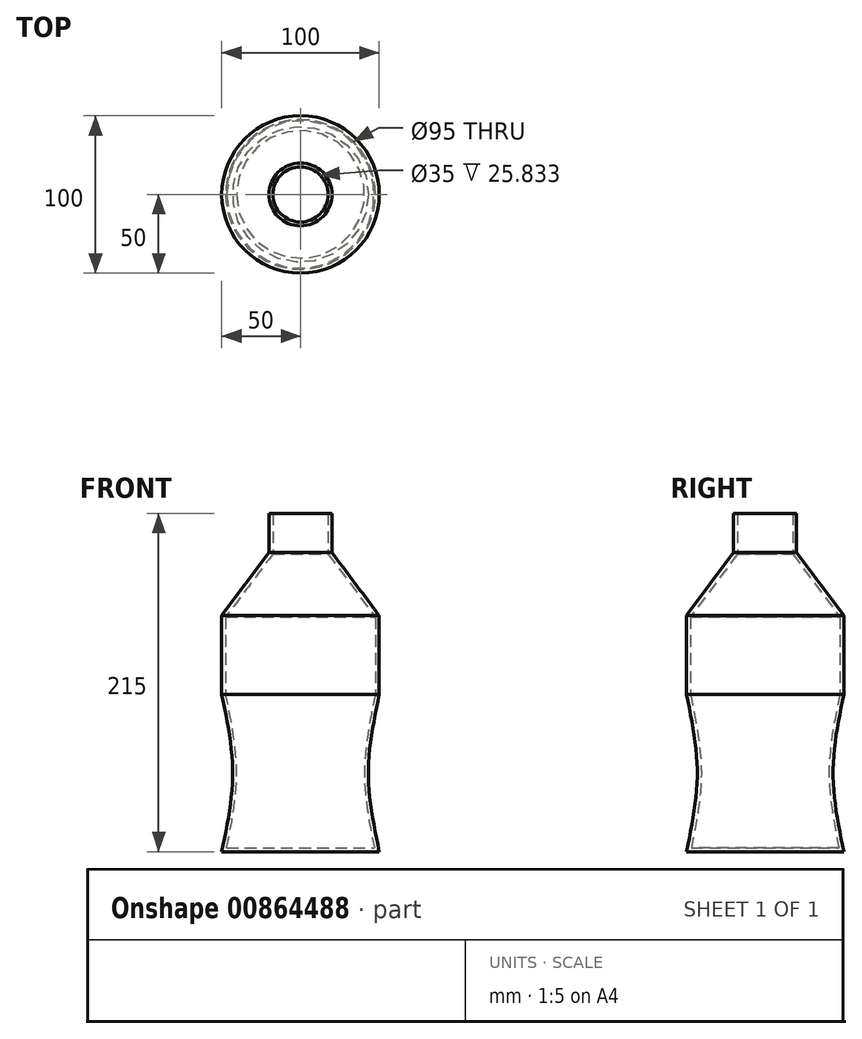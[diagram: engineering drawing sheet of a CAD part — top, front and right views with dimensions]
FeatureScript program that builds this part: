
annotation { "Feature Type Name" : "Feature", "Feature Type Description" : "" }
export const myFeature = defineFeature(function(context is Context, id is Id, definition is map)
    precondition{}
    {
        {
            var Q0;
            Q0=qCreatedBy(makeId("Top.planeOp"),FACE);
            var sketch = newSketch(context, id + "F0", { "sketchPlane" : qUnion([Q0])});
            skCircle(sketch, "E0", {"center": v(0, 0) * mm, "radius": 50 * mm});
            skSolve(sketch);
        }
        {
            var Q0;
            Q0=qCreatedBy(makeId("Top.planeOp"),FACE);
            cPlane(context, id + "F1", {"entities" : qUnion([Q0]), "cplaneType" : CPlaneType.OFFSET, "offset" : 50 * mm, "width" : 150 * mm, "height" : 150 * mm});
        }
        {
            var Q0;
            Q0=qCreatedBy(id+"F1.planeOp",FACE);
            var sketch = newSketch(context, id + "F2", { "sketchPlane" : qUnion([Q0])});
            skCircle(sketch, "E1", {"center": v(0, 0) * mm, "radius": 43.1 * mm});
            skSolve(sketch);
        }
        {
            var Q0;
            Q0=qCreatedBy(id+"F1.planeOp",FACE);
            cPlane(context, id + "F3", {"entities" : qUnion([Q0]), "cplaneType" : CPlaneType.OFFSET, "offset" : 50 * mm, "width" : 150 * mm, "height" : 150 * mm});
        }
        {
            var Q0;
            Q0=qCreatedBy(id+"F3.planeOp",FACE);
            cPlane(context, id + "F4", {"entities" : qUnion([Q0]), "cplaneType" : CPlaneType.OFFSET, "offset" : 50 * mm, "width" : 150 * mm, "height" : 150 * mm});
        }
        {
            var Q0;
            Q0=qCreatedBy(id+"F3.planeOp",FACE);
            var sketch = newSketch(context, id + "F5", { "sketchPlane" : qUnion([Q0])});
            skCircle(sketch, "E2", {"center": v(0, 0) * mm, "radius": 50 * mm});
            skSolve(sketch);
        }
        {
            var Q0;
            Q0=qCreatedBy(id+"F4.planeOp",FACE);
            var sketch = newSketch(context, id + "F6", { "sketchPlane" : qUnion([Q0])});
            skCircle(sketch, "E3", {"center": v(0, 0) * mm, "radius": 50 * mm});
            skSolve(sketch);
        }
        {
            var Q0;
            Q0=qCreatedBy(id+"F4.planeOp",FACE);
            cPlane(context, id + "F7", {"entities" : qUnion([Q0]), "cplaneType" : CPlaneType.OFFSET, "offset" : 40 * mm, "width" : 150 * mm, "height" : 150 * mm});
        }
        {
            var Q0;
            Q0=qCreatedBy(id+"F7.planeOp",FACE);
            var sketch = newSketch(context, id + "F8", { "sketchPlane" : qUnion([Q0])});
            skCircle(sketch, "E4", {"center": v(0, 0) * mm, "radius": 20 * mm});
            skSolve(sketch);
        }
        {
            var Q0;
            Q0=makeQuery(id+"F0.imprint","IMPRINT",FACE,{"disambiguationData":[TD([[makeQuery(id+"F0.imprint","IMPRINT",EDGE,{"derivedFrom":sQuery(id+"F0.wireOp",EDGE,"E0")}),1.0]])]});
            var Q1;
            Q1=makeQuery(id+"F2.imprint","IMPRINT",FACE,{"disambiguationData":[TD([[makeQuery(id+"F2.imprint","IMPRINT",EDGE,{"derivedFrom":sQuery(id+"F2.wireOp",EDGE,"E1")}),1.0]])]});
            var Q2;
            Q2=makeQuery(id+"F5.imprint","IMPRINT",FACE,{"disambiguationData":[TD([[makeQuery(id+"F5.imprint","IMPRINT",EDGE,{"derivedFrom":sQuery(id+"F5.wireOp",EDGE,"E2")}),1.0]])]});
            loft(context, id + "F9", {"sheetProfilesArray" : [{ "sheetProfileEntities" : qUnion([Q0]) }, { "sheetProfileEntities" : qUnion([Q1]) }, { "sheetProfileEntities" : qUnion([Q2]) }]});
        }
        {
            var Q0;
            Q0=makeQuery(id+"F5.imprint","IMPRINT",FACE,{"disambiguationData":[TD([[makeQuery(id+"F5.imprint","IMPRINT",EDGE,{"derivedFrom":sQuery(id+"F5.wireOp",EDGE,"E2")}),1.0]])]});
            extrude(context, id + "F10", {"entities" : qUnion([Q0]), "operationType" : NewBodyOperationType.ADD, "depth" : 50 * mm, "offsetDistance" : 25 * mm});
        }
        {
            var Q1;
            Q1=makeQuery(id+"F6.imprint","IMPRINT",FACE,{"disambiguationData":[TD([[makeQuery(id+"F6.imprint","IMPRINT",EDGE,{"derivedFrom":sQuery(id+"F6.wireOp",EDGE,"E3")}),1.0]])]});
            var Q2;
            Q2=makeQuery(id+"F8.imprint","IMPRINT",FACE,{"disambiguationData":[TD([[makeQuery(id+"F8.imprint","IMPRINT",EDGE,{"derivedFrom":sQuery(id+"F8.wireOp",EDGE,"E4")}),1.0]])]});
            loft(context, id + "F11", {"operationType" : NewBodyOperationType.ADD, "sheetProfilesArray" : [{ "sheetProfileEntities" : qUnion([Q1]) }, { "sheetProfileEntities" : qUnion([Q2]) }]});
        }
        {
            var Q0;
            Q0=makeQuery(id+"F11.opLoft","CAP_FACE",FACE,{"disambiguationData":[OSD([makeQuery(id+"F8.imprint","IMPRINT",FACE,{"disambiguationData":[TD([[makeQuery(id+"F8.imprint","IMPRINT",EDGE,{"derivedFrom":sQuery(id+"F8.wireOp",EDGE,"E4")}),1.0]])]})])],"isStart":true});
            extrude(context, id + "F12", {"entities" : qUnion([Q0]), "operationType" : NewBodyOperationType.ADD, "depth" : 25 * mm, "offsetDistance" : 25 * mm});
        }
        {
            var Q0;
            Q0=makeQuery(id+"F12.opExtrude","CAP_FACE",FACE,{"disambiguationData":[OSD([makeQuery(id+"F8.imprint","IMPRINT",FACE,{"disambiguationData":[TD([[makeQuery(id+"F8.imprint","IMPRINT",EDGE,{"derivedFrom":sQuery(id+"F8.wireOp",EDGE,"E4")}),1.0]])]})])],"isStart":false});
            shell(context, id + "F13", {"entities" : qUnion([Q0]), "thickness" : 2.5 * mm});
        }
    });
